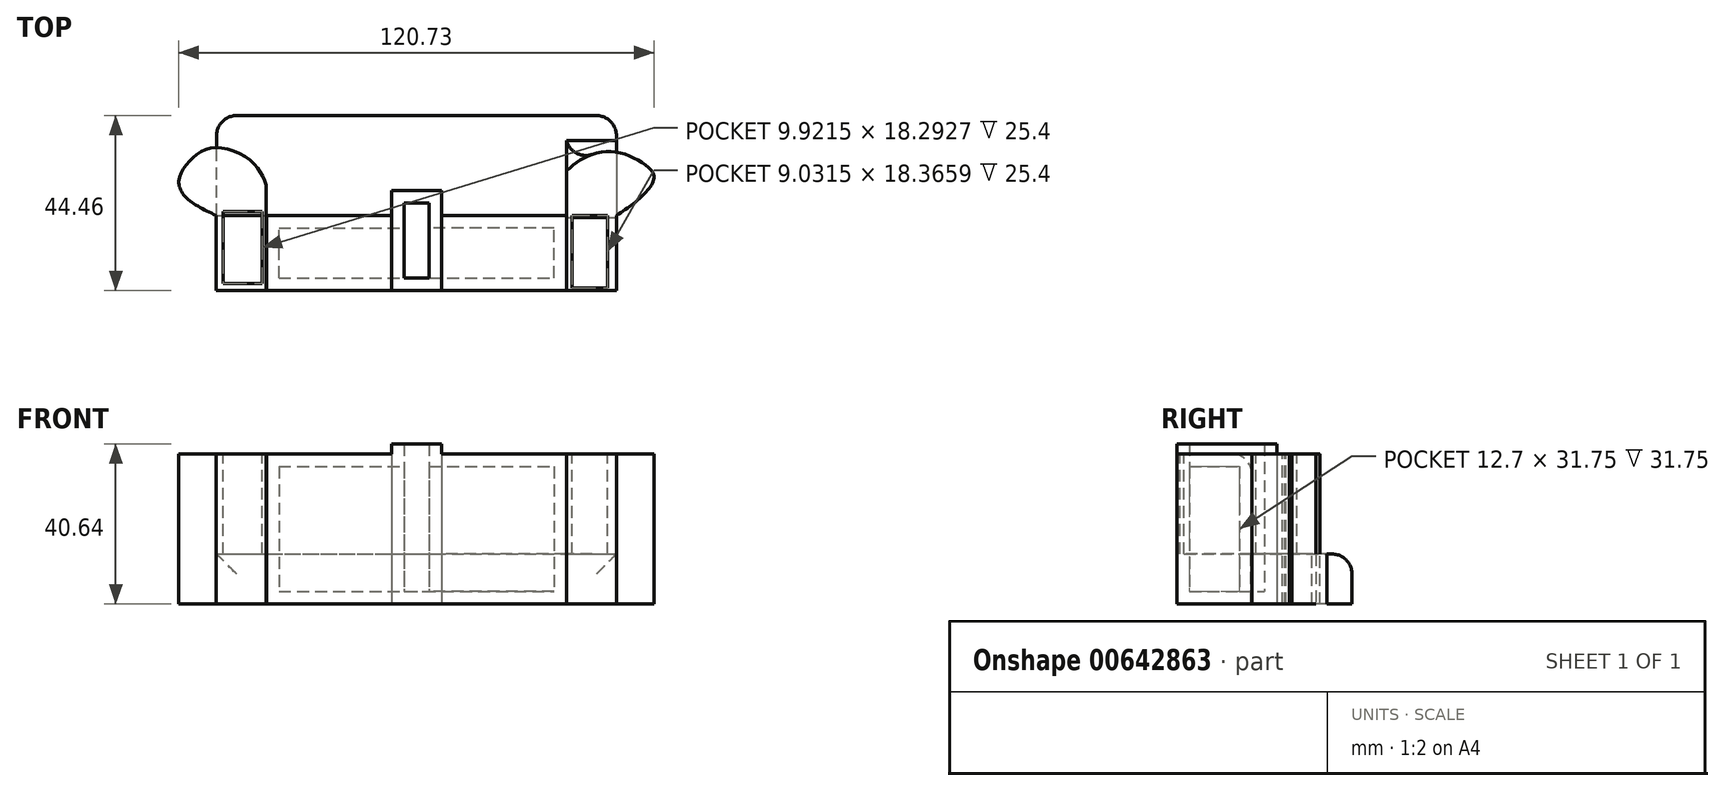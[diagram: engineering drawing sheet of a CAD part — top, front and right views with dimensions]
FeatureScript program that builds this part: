
annotation { "Feature Type Name" : "Feature", "Feature Type Description" : "" }
export const myFeature = defineFeature(function(context is Context, id is Id, definition is map)
    precondition{}
    {
        {
            var Q0;
            Q0=qCreatedBy(makeId("Top.planeOp"),FACE);
            var sketch = newSketch(context, id + "F0", { "sketchPlane" : qUnion([Q0])});
            skLineSegment(sketch, "E0", {"start": v(-44.05, -43.41) * mm, "end": v(-12.3, -43.41) * mm});
            skLineSegment(sketch, "E1", {"start": v(-12.3, -43.41) * mm, "end": v(0.4, -43.41) * mm});
            skLineSegment(sketch, "E2", {"start": v(0.4, -43.41) * mm, "end": v(32.15, -43.41) * mm});
            skLineSegment(sketch, "E3", {"start": v(-44.05, -43.41) * mm, "end": v(-56.75, -43.41) * mm});
            skLineSegment(sketch, "E4", {"start": v(32.15, -43.41) * mm, "end": v(44.85, -43.41) * mm});
            skLineSegment(sketch, "E5", {"start": v(-12.3, -43.41) * mm, "end": v(-12.3, -18.01) * mm});
            skLineSegment(sketch, "E6", {"start": v(0.4, -43.41) * mm, "end": v(0.4, -18.01) * mm});
            skLineSegment(sketch, "E7", {"start": v(-12.3, -18.01) * mm, "end": v(0.4, -18.01) * mm});
            skLineSegment(sketch, "E8", {"start": v(-44.05, -43.41) * mm, "end": v(-44.05, -24.36) * mm});
            skLineSegment(sketch, "E9", {"start": v(-44.05, -24.36) * mm, "end": v(-12.3, -24.36) * mm});
            skLineSegment(sketch, "E10", {"start": v(32.15, -43.41) * mm, "end": v(32.15, -24.36) * mm});
            skLineSegment(sketch, "E11", {"start": v(32.15, -24.36) * mm, "end": v(0, -24.36) * mm});
            skLineSegment(sketch, "E12", {"start": v(-44.05, -24.36) * mm, "end": v(-56.75, -24.36) * mm});
            skLineSegment(sketch, "E13", {"start": v(-56.75, -24.36) * mm, "end": v(-56.75, 1.04) * mm});
            skLineSegment(sketch, "E14", {"start": v(-56.75, 1.04) * mm, "end": v(44.85, 1.04) * mm});
            skLineSegment(sketch, "E15", {"start": v(32.15, -24.36) * mm, "end": v(44.85, -24.36) * mm});
            skLineSegment(sketch, "E16", {"start": v(44.85, 1.04) * mm, "end": v(44.85, -24.36) * mm});
            skSolve(sketch);
        }
        {
            var Q0;
            {var subQ1=sQuery(id+"F0.wireOp",EDGE,"E1");Q0=makeQuery(id+"F0.imprint","IMPRINT",FACE,{"disambiguationData":[TD([[makeQuery(id+"F0.imprint","IMPRINT",EDGE,{"derivedFrom":subQ1}),1.0]])]});}
            extrude(context, id + "F1", {"entities" : qUnion([Q0]), "depth" : 40.64 * mm, "offsetDistance" : 25.4 * mm});
        }
        {
            var Q0;
            {var subQ0=sQuery(id+"F0.wireOp",EDGE,"E0");Q0=makeQuery(id+"F0.imprint","IMPRINT",FACE,{"disambiguationData":[TD([[makeQuery(id+"F0.imprint","IMPRINT",EDGE,{"derivedFrom":subQ0}),1.0]])]});}
            var Q1;
            {var subQ0=sQuery(id+"F0.wireOp",EDGE,"E2");Q1=makeQuery(id+"F0.imprint","IMPRINT",FACE,{"disambiguationData":[TD([[makeQuery(id+"F0.imprint","IMPRINT",EDGE,{"derivedFrom":subQ0}),1.0]])]});}
            extrude(context, id + "F2", {"entities" : qUnion([Q0, Q1]), "operationType" : NewBodyOperationType.ADD, "depth" : 38.1 * mm, "offsetDistance" : 25.4 * mm});
        }
        {
            var Q0;
            Q0=makeQuery(id+"F1.opExtrude","CAP_FACE",FACE,{"disambiguationData":[OSD([sQuery(id+"F0.wireOp",EDGE,"E1"),sQuery(id+"F0.wireOp",EDGE,"E5"),sQuery(id+"F0.wireOp",EDGE,"E6"),sQuery(id+"F0.wireOp",EDGE,"E7")])],"isStart":false});
            shell(context, id + "F3", {"entities" : qUnion([Q0]), "thickness" : 3.17 * mm});
        }
        {
            var Q0;
            Q0=qCreatedBy(makeId("Top.planeOp"),FACE);
            var sketch = newSketch(context, id + "F4", { "sketchPlane" : qUnion([Q0])});
            skLineSegment(sketch, "E17", {"start": v(-44.11, -43.4) * mm, "end": v(-56.81, -43.4) * mm});
            skLineSegment(sketch, "E18", {"start": v(-56.81, -43.4) * mm, "end": v(-56.81, -24.36) * mm});
            skLineSegment(sketch, "E19", {"start": v(-56.81, -24.36) * mm, "end": v(-66.34, -24.36) * mm});
            skLineSegment(sketch, "E20", {"start": v(-66.34, -24.36) * mm, "end": v(-66.34, -5.3) * mm});
            skLineSegment(sketch, "E21", {"start": v(-66.34, -5.3) * mm, "end": v(-44.11, -5.3) * mm});
            skLineSegment(sketch, "E22", {"start": v(-44.11, -43.4) * mm, "end": v(-44.11, -12.93) * mm});
            skLineSegment(sketch, "E23", {"start": v(-44.11, -12.93) * mm, "end": v(-44.11, -5.3) * mm});
            skSolve(sketch);
        }
        {
            var Q0;
            Q0=makeQuery(id+"F4.imprint","IMPRINT",FACE,{"disambiguationData":[TD([[makeQuery(id+"F4.imprint","IMPRINT",EDGE,{"derivedFrom":sQuery(id+"F4.wireOp",EDGE,"57a20458-bb52-455f-a131-d67d1a580d390.MirrorCS")}),-1.0]])]});
            var Q1;
            Q1=makeQuery(id+"F4.imprint","IMPRINT",FACE,{"disambiguationData":[TD([[makeQuery(id+"F4.imprint","IMPRINT",EDGE,{"derivedFrom":sQuery(id+"F4.wireOp",EDGE,"E17")}),-1.0]])]});
            extrude(context, id + "F5", {"entities" : qUnion([Q0, Q1]), "depth" : 38.1 * mm, "offsetDistance" : 25.4 * mm});
        }
        {
            var Q0;
            Q0=makeQuery(id+"F5.opExtrude","CAP_FACE",FACE,{"disambiguationData":[OSD([sQuery(id+"F4.wireOp",EDGE,"E17"),sQuery(id+"F4.wireOp",EDGE,"E18"),sQuery(id+"F4.wireOp",EDGE,"E19"),sQuery(id+"F4.wireOp",EDGE,"E20"),sQuery(id+"F4.wireOp",EDGE,"E21"),sQuery(id+"F4.wireOp",EDGE,"E22"),sQuery(id+"F4.wireOp",EDGE,"E23")])],"isStart":false});
            var sketch = newSketch(context, id + "F6", { "sketchPlane" : qUnion([Q0])});
            skFitSpline(sketch, "E24", {"points": [v(-56.81, -24.36) * mm, v(-64.1, -20.13) * mm, v(-66.34, -15.7) * mm, v(-63.49, -10.43) * mm, v(-57.3, -7.14) * mm, v(-47.76, -10.7) * mm, v(-44.11, -16.62) * mm], "startDerivative": vector(-45.12, 21.14) * mm, "endDerivative": vector(15.33, -38.07) * mm});
            skLineSegment(sketch, "E25", {"start": v(-44.11, -16.62) * mm, "end": v(-44.11, -43.4) * mm});
            skFitSpline(sketch, "E26.MirrorCS", {"points": [v(44.85, -24.36) * mm, v(52.13, -20.13) * mm, v(54.38, -15.7) * mm, v(51.53, -10.43) * mm, v(45.34, -7.14) * mm, v(35.8, -10.7) * mm, v(32.15, -16.62) * mm], "startDerivative": vector(45.12, 21.14) * mm, "endDerivative": vector(-15.33, -38.07) * mm});
            skSolve(sketch);
        }
        {
            var Q0;
            {var subQ5=makeQuery(id+"F5.opExtrude","CAP_EDGE",EDGE,{"disambiguationData":[OSD([sQuery(id+"F4.wireOp",EDGE,"E21")])],"isStart":false});Q0=makeQuery(id+"F6.imprint","IMPRINT",FACE,{"disambiguationData":[TD([[makeQuery(id+"F6.imprint","IMPRINT",EDGE,{"derivedFrom":subQ5}),-1.0]])]});}
            var Q1;
            {var subQ1=makeQuery(id+"F5.opExtrude","CAP_EDGE",EDGE,{"disambiguationData":[OSD([sQuery(id+"F4.wireOp",EDGE,"E19")])],"isStart":false});Q1=makeQuery(id+"F6.imprint","IMPRINT",FACE,{"disambiguationData":[TD([[makeQuery(id+"F6.imprint","IMPRINT",EDGE,{"derivedFrom":subQ1}),-1.0]])]});}
            extrude(context, id + "F7", {"entities" : qUnion([Q0, Q1]), "operationType" : NewBodyOperationType.REMOVE, "oppositeDirection" : true, "depth" : 38.1 * mm, "offsetDistance" : 25.4 * mm});
        }
        {
            var Q0;
            {var subQ0=sQuery(id+"F0.wireOp",EDGE,"E7");Q0=makeQuery(id+"F0.imprint","IMPRINT",FACE,{"disambiguationData":[TD([[makeQuery(id+"F0.imprint","IMPRINT",EDGE,{"derivedFrom":subQ0}),1.0]])]});}
            extrude(context, id + "F8", {"entities" : qUnion([Q0]), "depth" : 12.7 * mm, "offsetDistance" : 25.4 * mm});
        }
        {
            var Q0;
            Q0=qCreatedBy(makeId("Top.planeOp"),FACE);
            var sketch = newSketch(context, id + "F9", { "sketchPlane" : qUnion([Q0])});
            skLineSegment(sketch, "E27", {"start": v(32.16, -43.42) * mm, "end": v(44.86, -43.42) * mm});
            skLineSegment(sketch, "E28", {"start": v(44.86, -43.42) * mm, "end": v(44.86, -24.37) * mm});
            skLineSegment(sketch, "E29", {"start": v(32.16, -43.42) * mm, "end": v(32.16, -12.94) * mm});
            skLineSegment(sketch, "E30", {"start": v(44.86, -24.37) * mm, "end": v(54.39, -24.37) * mm});
            skLineSegment(sketch, "E31", {"start": v(54.39, -24.37) * mm, "end": v(54.39, -5.32) * mm});
            skLineSegment(sketch, "E32", {"start": v(54.39, -5.32) * mm, "end": v(32.16, -5.32) * mm});
            skLineSegment(sketch, "E33", {"start": v(32.16, -12.94) * mm, "end": v(32.16, -5.32) * mm});
            skSolve(sketch);
        }
        {
            var Q0;
            Q0=makeQuery(id+"F9.imprint","IMPRINT",FACE,{"disambiguationData":[TD([[makeQuery(id+"F9.imprint","IMPRINT",EDGE,{"derivedFrom":sQuery(id+"F9.wireOp",EDGE,"E27")}),1.0]])]});
            extrude(context, id + "F10", {"entities" : qUnion([Q0]), "operationType" : NewBodyOperationType.ADD, "depth" : 38.1 * mm, "offsetDistance" : 25.4 * mm});
        }
        {
            var Q0;
            Q0=makeQuery(id+"F10.opExtrude","CAP_FACE",FACE,{"disambiguationData":[OSD([sQuery(id+"F9.wireOp",EDGE,"E27"),sQuery(id+"F9.wireOp",EDGE,"E28"),sQuery(id+"F9.wireOp",EDGE,"E29"),sQuery(id+"F9.wireOp",EDGE,"E30"),sQuery(id+"F9.wireOp",EDGE,"E31"),sQuery(id+"F9.wireOp",EDGE,"E32"),sQuery(id+"F9.wireOp",EDGE,"E33")])],"isStart":false});
            var sketch = newSketch(context, id + "F11", { "sketchPlane" : qUnion([Q0])});
            skFitSpline(sketch, "E34", {"points": [v(32.16, -12.94) * mm, v(37.4, -9.34) * mm, v(44.59, -8.24) * mm, v(51.5, -11) * mm, v(54.39, -14.28) * mm, v(51.96, -18.84) * mm, v(44.86, -24.37) * mm], "startDerivative": vector(29.53, 24.5) * mm, "endDerivative": vector(-39.46, -26.99) * mm});
            skSolve(sketch);
        }
        {
            var Q0;
            {var subQ5=makeQuery(id+"F10.opExtrude","CAP_EDGE",EDGE,{"disambiguationData":[OSD([sQuery(id+"F9.wireOp",EDGE,"E32")])],"isStart":false});Q0=makeQuery(id+"F11.imprint","IMPRINT",FACE,{"disambiguationData":[TD([[makeQuery(id+"F11.imprint","IMPRINT",EDGE,{"derivedFrom":subQ5}),1.0]])]});}
            var Q1;
            {var subQ1=makeQuery(id+"F10.opExtrude","CAP_EDGE",EDGE,{"disambiguationData":[OSD([sQuery(id+"F9.wireOp",EDGE,"E30")])],"isStart":false});Q1=makeQuery(id+"F11.imprint","IMPRINT",FACE,{"disambiguationData":[TD([[makeQuery(id+"F11.imprint","IMPRINT",EDGE,{"derivedFrom":subQ1}),1.0]])]});}
            extrude(context, id + "F12", {"entities" : qUnion([Q0, Q1]), "operationType" : NewBodyOperationType.REMOVE, "oppositeDirection" : true, "depth" : 38.1 * mm, "offsetDistance" : 25.4 * mm});
        }
        {
            var Q0;
            Q0=qCreatedBy(makeId("Top.planeOp"),FACE);
            var sketch = newSketch(context, id + "F13", { "sketchPlane" : qUnion([Q0])});
            skLineSegment(sketch, "E35.bottom", {"start": v(32.14, -5.29) * mm, "end": v(44.86, -5.29) * mm});
            skLineSegment(sketch, "E35.top", {"start": v(32.14, -24.82) * mm, "end": v(44.86, -24.82) * mm});
            skLineSegment(sketch, "E35.left", {"start": v(32.14, -5.29) * mm, "end": v(32.14, -24.82) * mm});
            skLineSegment(sketch, "E35.right", {"start": v(44.86, -5.29) * mm, "end": v(44.86, -24.82) * mm});
            skSolve(sketch);
        }
        {
            var Q0;
            Q0=makeQuery(id+"F13.imprint","IMPRINT",FACE,{"disambiguationData":[TD([[makeQuery(id+"F13.imprint","IMPRINT",EDGE,{"derivedFrom":sQuery(id+"F13.wireOp",EDGE,"E35.bottom")}),-1.0]])]});
            extrude(context, id + "F14", {"entities" : qUnion([Q0]), "depth" : 12.7 * mm, "offsetDistance" : 25.4 * mm});
        }
        {
            var Q0;
            Q0=makeQuery(id+"F5.opExtrude","CAP_FACE",FACE,{"disambiguationData":[OSD([sQuery(id+"F4.wireOp",EDGE,"E17"),sQuery(id+"F4.wireOp",EDGE,"E18"),sQuery(id+"F4.wireOp",EDGE,"E19"),sQuery(id+"F4.wireOp",EDGE,"E20"),sQuery(id+"F4.wireOp",EDGE,"E21"),sQuery(id+"F4.wireOp",EDGE,"E22"),sQuery(id+"F4.wireOp",EDGE,"E23")])],"isStart":false});
            var sketch = newSketch(context, id + "F15", { "sketchPlane" : qUnion([Q0])});
            skLineSegment(sketch, "E36.bottom", {"start": v(-55.08, -41.63) * mm, "end": v(-45.16, -41.63) * mm});
            skLineSegment(sketch, "E36.top", {"start": v(-55.08, -23.33) * mm, "end": v(-45.16, -23.33) * mm});
            skLineSegment(sketch, "E36.left", {"start": v(-55.08, -41.63) * mm, "end": v(-55.08, -23.33) * mm});
            skLineSegment(sketch, "E36.right", {"start": v(-45.16, -41.63) * mm, "end": v(-45.16, -23.33) * mm});
            skSolve(sketch);
        }
        {
            var Q0;
            Q0=makeQuery(id+"F15.imprint","IMPRINT",FACE,{"disambiguationData":[TD([[makeQuery(id+"F15.imprint","IMPRINT",EDGE,{"derivedFrom":sQuery(id+"F15.wireOp",EDGE,"E36.bottom")}),1.0]])]});
            extrude(context, id + "F16", {"entities" : qUnion([Q0]), "operationType" : NewBodyOperationType.REMOVE, "oppositeDirection" : true, "depth" : 25.4 * mm, "offsetDistance" : 25.4 * mm});
        }
        {
            var Q0;
            Q0=makeQuery(id+"F10.opExtrude","CAP_FACE",FACE,{"disambiguationData":[OSD([sQuery(id+"F9.wireOp",EDGE,"E27"),sQuery(id+"F9.wireOp",EDGE,"E28"),sQuery(id+"F9.wireOp",EDGE,"E29"),sQuery(id+"F9.wireOp",EDGE,"E30"),sQuery(id+"F9.wireOp",EDGE,"E31"),sQuery(id+"F9.wireOp",EDGE,"E32"),sQuery(id+"F9.wireOp",EDGE,"E33")])],"isStart":false});
            var sketch = newSketch(context, id + "F17", { "sketchPlane" : qUnion([Q0])});
            skLineSegment(sketch, "E37.bottom", {"start": v(33.59, -24.38) * mm, "end": v(42.62, -24.38) * mm});
            skLineSegment(sketch, "E37.top", {"start": v(33.59, -42.74) * mm, "end": v(42.62, -42.74) * mm});
            skLineSegment(sketch, "E37.left", {"start": v(33.59, -24.38) * mm, "end": v(33.59, -42.74) * mm});
            skLineSegment(sketch, "E37.right", {"start": v(42.62, -24.38) * mm, "end": v(42.62, -42.74) * mm});
            skSolve(sketch);
        }
        {
            var Q0;
            Q0=makeQuery(id+"F17.imprint","IMPRINT",FACE,{"disambiguationData":[TD([[makeQuery(id+"F17.imprint","IMPRINT",EDGE,{"derivedFrom":sQuery(id+"F17.wireOp",EDGE,"E37.bottom")}),-1.0]])]});
            extrude(context, id + "F18", {"entities" : qUnion([Q0]), "operationType" : NewBodyOperationType.REMOVE, "oppositeDirection" : true, "depth" : 25.4 * mm, "offsetDistance" : 25.4 * mm});
        }
        {
            var Q0;
            Q0=makeQuery(id+"F2.opExtrude","CAP_EDGE",EDGE,{"disambiguationData":[OSD([sQuery(id+"F0.wireOp",EDGE,"E9")])],"isStart":false});
            var Q1;
            Q1=makeQuery(id+"F2.opExtrude","CAP_EDGE",EDGE,{"disambiguationData":[OSD([sQuery(id+"F0.wireOp",EDGE,"E11")])],"isStart":false});
            var Q2;
            Q2=makeQuery(id+"F8.opExtrude","CAP_EDGE",EDGE,{"disambiguationData":[OSD([sQuery(id+"F0.wireOp",EDGE,"E14")])],"isStart":false});
            var Q3;
            Q3=makeQuery(id+"F8.opExtrude","SWEPT_EDGE",EDGE,{"disambiguationData":[OSD([sQuery(id+"F0.wireOp",EDGE,"E14"),sQuery(id+"F0.wireOp",EDGE,"E16")])]});
            var Q4;
            Q4=makeQuery(id+"F8.opExtrude","SWEPT_EDGE",EDGE,{"disambiguationData":[OSD([sQuery(id+"F0.wireOp",EDGE,"E13"),sQuery(id+"F0.wireOp",EDGE,"E14")])]});
            var Q5;
            {var subQ0=sQuery(id+"F6.wireOp",EDGE,"E24");var subQ1=sQuery(id+"F4.wireOp",EDGE,"E20");Q5=makeQuery(id+"F7.boolean.opBoolean","COPY",EDGE,{"derivedFrom":makeQuery(id+"F7.opExtrude","SWEPT_EDGE",EDGE,{"disambiguationData":[OSD([subQ1,subQ0]),TDD([makeQuery(id+"F6.imprint","INTERSECT",VERTEX,{"disambiguationData":[OD(0.0)],"derivedFrom":[makeQuery(id+"F5.opExtrude","CAP_EDGE",EDGE,{"disambiguationData":[OSD([subQ1])],"isStart":false}),subQ0]})])]})});}
            var Q6;
            {var subQ0=sQuery(id+"F6.wireOp",EDGE,"E24");var subQ1=sQuery(id+"F4.wireOp",EDGE,"E20");Q6=makeQuery(id+"F7.boolean.opBoolean","COPY",EDGE,{"derivedFrom":makeQuery(id+"F7.opExtrude","SWEPT_EDGE",EDGE,{"disambiguationData":[OSD([subQ1,subQ0]),TDD([makeQuery(id+"F6.imprint","INTERSECT",VERTEX,{"disambiguationData":[OD(1.0)],"derivedFrom":[makeQuery(id+"F5.opExtrude","CAP_EDGE",EDGE,{"disambiguationData":[OSD([subQ1])],"isStart":false}),subQ0]})])]})});}
            var Q7;
            {var subQ0=sQuery(id+"F11.wireOp",EDGE,"E34");var subQ1=sQuery(id+"F9.wireOp",EDGE,"E31");Q7=makeQuery(id+"F12.boolean.opBoolean","COPY",EDGE,{"derivedFrom":makeQuery(id+"F12.opExtrude","SWEPT_EDGE",EDGE,{"disambiguationData":[OSD([subQ1,subQ0]),TDD([makeQuery(id+"F11.imprint","INTERSECT",VERTEX,{"disambiguationData":[OD(1.0)],"derivedFrom":[makeQuery(id+"F10.opExtrude","CAP_EDGE",EDGE,{"disambiguationData":[OSD([subQ1])],"isStart":false}),subQ0]})])]})});}
            var Q8;
            Q8=makeQuery(id+"F7.boolean.opBoolean","COPY",EDGE,{"derivedFrom":makeQuery(id+"F7.opExtrude","SWEPT_EDGE",EDGE,{"disambiguationData":[OSD([sQuery(id+"F4.wireOp",EDGE,"E22"),sQuery(id+"F4.wireOp",EDGE,"E23"),sQuery(id+"F6.wireOp",EDGE,"E24"),sQuery(id+"F6.wireOp",EDGE,"E25")])]})});
            var Q9;
            {var subQ0=sQuery(id+"F9.wireOp",EDGE,"E33");var subQ1=sQuery(id+"F9.wireOp",EDGE,"E29");var subQ2=sQuery(id+"F11.wireOp",EDGE,"E34");Q9=makeQuery(id+"F12.boolean.opBoolean","COPY",EDGE,{"disambiguationData":[topologyDisambiguationEdgeConnected([makeQuery(id+"F10.opExtrude","SWEPT_FACE",FACE,{"disambiguationData":[OSD([subQ1,subQ0])]})])],"derivedFrom":makeQuery(id+"F12.opExtrude","SWEPT_EDGE",EDGE,{"disambiguationData":[OSD([subQ1,subQ0,subQ2])]})});}
            fillet(context, id + "F19", {"entities" : qUnion([Q0, Q1, Q2, Q3, Q4, Q5, Q6, Q7, Q8, Q9]), "radius" : 5.08 * mm, "tangentPropagation" : true, "allowEdgeOverflow" : false});
        }
    });
